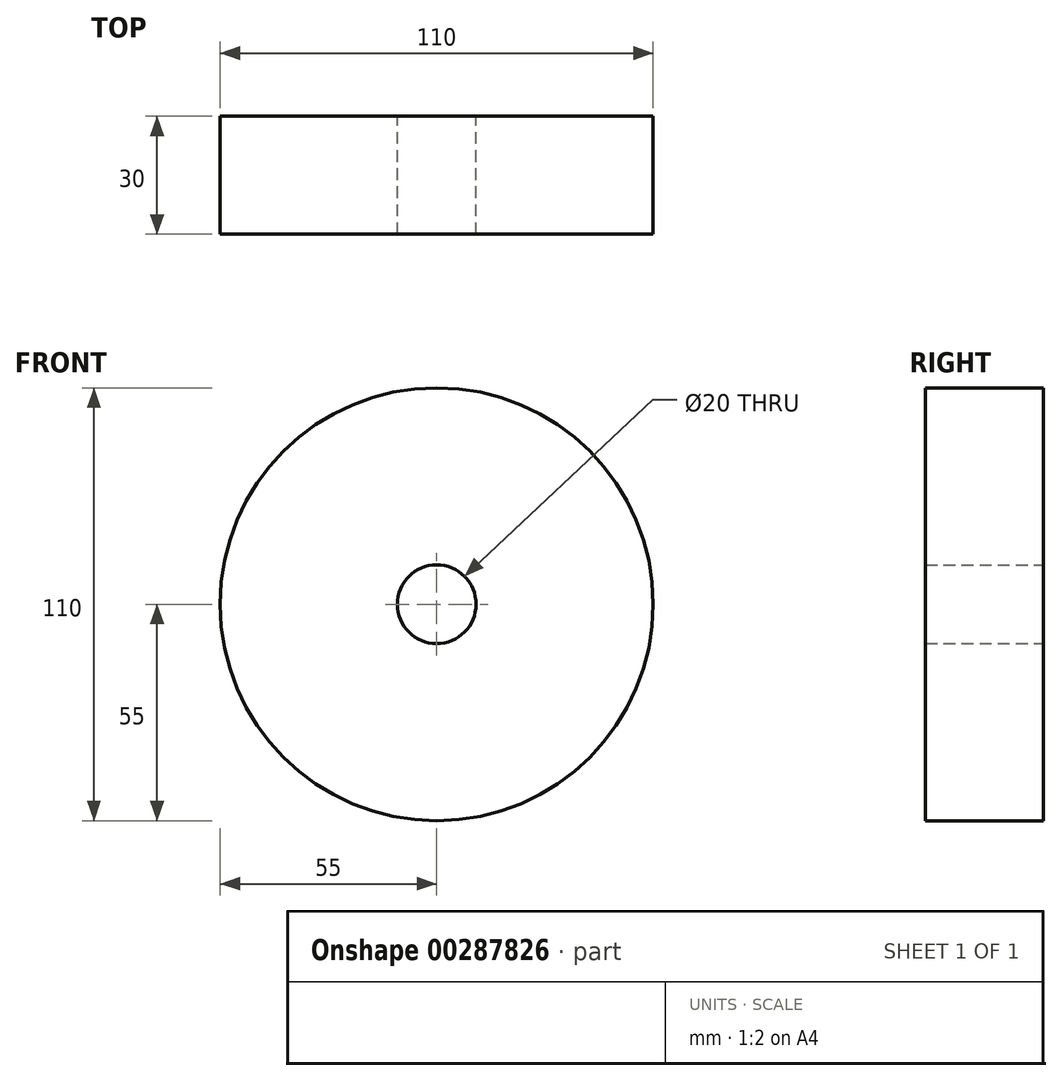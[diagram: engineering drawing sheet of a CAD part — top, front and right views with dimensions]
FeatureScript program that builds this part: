
annotation { "Feature Type Name" : "Feature", "Feature Type Description" : "" }
export const myFeature = defineFeature(function(context is Context, id is Id, definition is map)
    precondition{}
    {
        {
            var Q0;
            Q0=qCreatedBy(makeId("Front.planeOp"),FACE);
            var sketch = newSketch(context, id + "F0", { "sketchPlane" : qUnion([Q0])});
            skCircle(sketch, "E0", {"center": v(0, 0) * mm, "radius": 10 * mm});
            skCircle(sketch, "E1", {"center": v(0, 0) * mm, "radius": 55 * mm});
            skSolve(sketch);
        }
        {
            var Q0;
            Q0=makeQuery(id+"F0.imprint","IMPRINT",FACE,{"disambiguationData":[TD([[makeQuery(id+"F0.imprint","IMPRINT",EDGE,{"derivedFrom":sQuery(id+"F0.wireOp",EDGE,"E0")}),-1.0]])]});
            extrude(context, id + "F1", {"entities" : qUnion([Q0]), "depth" : 30 * mm});
        }
    });
